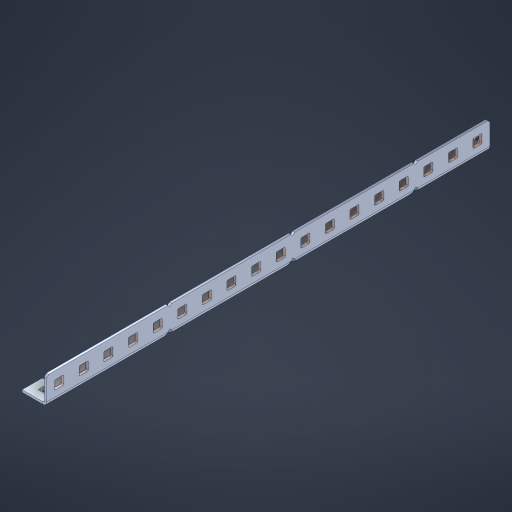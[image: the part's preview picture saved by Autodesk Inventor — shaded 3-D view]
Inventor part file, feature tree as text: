
AUTODESK INVENTOR PART (.ipt)
format: ipt  version: 2023 (Build 270158000, 158)  size: 887,296 bytes
history: native  units: in
note: dims shown in document units (in); Inventor stores cm internally (conversion verified against a paired STEP export)
features: other x61, extrude x52, sheet_metal_op x11, sketch x10, pattern_linear x2, mirror x1, chamfer x1
ambient origin geometry x8: Origin, YZ Plane, XZ Plane, XY Plane, X Axis, Y Axis, Z Axis, Center Point
bodies: Solid1 (feature_tree), Body (feature_tree)
feature tree (138):
  sheet_metal_op  "Flanges"
  other  "Flange Pattern Plane"
  other  "Flange Pattern Sketch"
  sheet_metal_op  "Flange Pattern"
  sheet_metal_op  "Body Pattern"
  pattern_linear  "Center Pattern"  Spacing1=0.0469in  [1 undecoded]
  other  "Arc Length"
  mirror  "Notch Mirror"
  pattern_linear  "Notch Pattern"  Spacing1=0.182in  [1 undecoded]
  chamfer  "End Chamfer"
  extrude  "Half Cut"  Depth=0.02in
  sketch  "Sketch1"  dims[d0=1.0in]
  other  "Plate1"
  sketch  "Sketch2"  dims[d1=9.0in]
  other  "Plate2"
  sheet_metal_op  "Bend1"
  sheet_metal_op  "Corner1"
  sketch  "Sketch3"  dims[d2=0.0469in]
  sketch  "Sketch7"  dims[d3=0.0469in]
  other  "Srf1"
  other  "Srf2"
  sketch  "Sketch8"  dims[d4=0.0234in]
  sketch  "Sketch9"  dims[d5=0.0938in]
  other  "Srf91"
  sheet_metal_op  "Body Pattern Sketch"
  other  "Srf92"
  sketch  "Sketch13"  dims[d6=0.0469in]
  sketch  "Sketch14"  dims[d7=0.5in d8=90.0deg d9=0.0312in]
  sketch  "Sketch15"  dims[d10=0.1875in]
  sketch  "Sketch16"  dims[d11=0.0469in d12=0.0469in d16=0.182in d17=0.02in d18=0.0469in d19=0.0in d20=0.25in d21=0.25in d38=7.0866in d40=0.5in d41=0.3937in d43=1.0in d46=0.172in d47=1.0in d48=0.0in d49=0.182in d50=0.02in d51=0.25in d52=0.25in d53=0.0469in d54=0.0in d55=0.172in d56=1.0in d57=0.0in d58=0.25in d60=7.0866in d62=0.5in d63=0.3937in d65=0.5in d85=0.1227in d86=0.1659in d88=0.04in d89=0.0469in d90=0.0in d91=0.04in d92=0.0491in d95=2.5in d96=0.04in d97=0.25in d98=45.0deg d99=0.25in d100=0.5in d101=0.0in d102=2.497in d106=0.182in d107=0.02in d108=0.5in d109=0.5in d110=0.0469in d111=0.0in d112=0.172in d113=0.5in d114=0.0in d117=0.5in d118=0.5in d119=0.5in]
  other  "Srf786"
  other  "Srf823"
  other  "Srf824"
  other  "Srf825"
  other  "Srf826"
  other  "Srf827"
  other  "Srf828"
  other  "Srf829"
  other  "Srf856"
  other  "Srf857"
  other  "Srf858"
  other  "Srf859"
  other  "Srf860"
  other  "Srf861"
  other  "Srf862"
  other  "Srf889"
  other  "Srf890"
  other  "Srf891"
  other  "Srf892"
  other  "Srf893"
  other  "Srf894"
  other  "Srf895"
  other  "Srf896"
  other  "Srf922"
  other  "Srf923"
  other  "Srf924"
  other  "Srf925"
  other  "Srf926"
  other  "Srf959"
  other  "Srf960"
  other  "Srf961"
  other  "Srf962"
  other  "Srf963"
  other  "Srf996"
  other  "Srf997"
  other  "Srf998"
  other  "Srf999"
  other  "Srf1000"
  other  "Srf1143"
  other  "Srf1144"
  other  "Srf1145"
  other  "Srf1146"
  other  "Srf1199"
  other  "Srf1200"
  other  "Srf1201"
  other  "Srf1202"
  other  "Srf1255"
  other  "Srf1256"
  other  "Srf1257"
  other  "Srf1258"
  sheet_metal_op  "Flange Stamp"
  sheet_metal_op  "Flange Circle"
  sheet_metal_op  "Body Stamp"
  sheet_metal_op  "Body Circle"
  other  "Center Stamp"
  other  "Center Circle"
  sheet_metal_op  "Notch"
  extrude  "ExtrusionSrf2"  Depth=0.0469in
  extrude  "ExtrusionSrf92"  TaperAngle=0.0deg  [1 undecoded]
  extrude  "ExtrusionSrf823"  Depth=0.25in
  extrude  "ExtrusionSrf824"  Depth=0.25in
  extrude  "ExtrusionSrf825"  Depth=0.5in
  extrude  "ExtrusionSrf826"  Depth=0.5in
  extrude  "ExtrusionSrf827"  Depth=1.0in TaperAngle=0.0deg
  extrude  "ExtrusionSrf828"  Depth=0.182in
  extrude  "ExtrusionSrf829"  Depth=0.02in
  extrude  "ExtrusionSrf856"  Depth=0.25in
  extrude  "ExtrusionSrf857"  Depth=0.25in
  extrude  "ExtrusionSrf858"  Depth=0.0469in
  extrude  "ExtrusionSrf859"  TaperAngle=0.0deg  [1 undecoded]
  extrude  "ExtrusionSrf860"  Depth=0.5in
  extrude  "ExtrusionSrf861"  Depth=1.0in TaperAngle=0.0deg
  extrude  "ExtrusionSrf862"  Depth=0.25in
  extrude  "ExtrusionSrf889"  Depth=0.5in
  extrude  "ExtrusionSrf890"  Depth=0.5in
  extrude  "ExtrusionSrf891"  Depth=0.5in
  extrude  "ExtrusionSrf892"  Depth=0.5in
  extrude  "ExtrusionSrf893"  Depth=0.5in
  extrude  "ExtrusionSrf894"  Depth=0.0469in
  extrude  "ExtrusionSrf895"  TaperAngle=0.0deg  [1 undecoded]
  extrude  "ExtrusionSrf896"  Depth=0.5in
  extrude  "ExtrusionSrf922"  Depth=0.5in
  extrude  "ExtrusionSrf923"  Depth=2.5in
  extrude  "ExtrusionSrf924"  Depth=0.25in TaperAngle=45.0deg
  extrude  "ExtrusionSrf925"  Depth=0.25in
  extrude  "ExtrusionSrf926"  Depth=0.5in TaperAngle=0.0deg
  extrude  "ExtrusionSrf959"  Depth=0.5in
  extrude  "ExtrusionSrf960"  Depth=0.182in
  extrude  "ExtrusionSrf961"  Depth=0.02in
  extrude  "ExtrusionSrf962"  Depth=0.5in
  extrude  "ExtrusionSrf963"  Depth=0.5in
  extrude  "ExtrusionSrf996"  Depth=0.0469in
  extrude  "ExtrusionSrf997"  TaperAngle=0.0deg  [1 undecoded]
  extrude  "ExtrusionSrf998"  Depth=0.5in
  extrude  "ExtrusionSrf999"  Depth=0.5in TaperAngle=0.0deg
  extrude  "ExtrusionSrf1000"  Depth=0.5in
  extrude  "ExtrusionSrf1143"  Depth=0.5in
  extrude  "ExtrusionSrf1144"  Depth=0.5in
  extrude  "ExtrusionSrf1145"  [1 undecoded]
  extrude  "ExtrusionSrf1146"  [1 undecoded]
  extrude  "ExtrusionSrf1199"  [1 undecoded]
  extrude  "ExtrusionSrf1200"  [1 undecoded]
  extrude  "ExtrusionSrf1201"  [1 undecoded]
  extrude  "ExtrusionSrf1202"  [1 undecoded]
  extrude  "ExtrusionSrf1255"  [1 undecoded]
  extrude  "ExtrusionSrf1256"  [1 undecoded]
  extrude  "ExtrusionSrf1257"  [1 undecoded]
  extrude  "ExtrusionSrf1258"  [1 undecoded]
note: 16 required parameter values undecoded (feature->parameter linkage not recoverable at this tier; creation-order binding heuristic only, values carry confidence <= 0.55)
